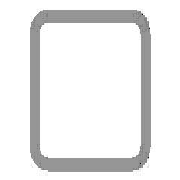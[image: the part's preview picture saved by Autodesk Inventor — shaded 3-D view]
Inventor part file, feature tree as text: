
AUTODESK INVENTOR PART (.ipt)
format: ipt  version: 2024 (Build 280153000, 153)  size: 128,512 bytes
history: native  units: mm (DEFAULTED — no unit token found)
features: other x4, extrude x1, sketch x1, plane x1
ambient origin geometry x8: Origin, YZ Plane, XZ Plane, XY Plane, X Axis, Y Axis, Z Axis, Center Point
bodies: Solid1 (feature_tree)
feature tree (7):
  parser-record x1  (decoder bookkeeping rows leaked as tree rows — omitted from the tree; the rows remain in map.json)
  other  "Driven Length"
  other  "Plano inicial"
  other  "Plano final"
  extrude  "Cuerpo"  TaperAngle=0.0deg  [1 undecoded]
  sketch  "Sketch3"  dims[d3=2890.0mm d4=0.0mm d10=50.8mm d11=50.8mm d12=3.175mm d13=-0.0mm d14=2890.0mm d15=25.4mm d16=25.4mm d17=6.35mm d18=90.0deg d19=2890.0mm]
  plane  "Work Plane3"
note: 1 required parameter value undecoded (feature->parameter linkage not recoverable at this tier; creation-order binding heuristic only, values carry confidence <= 0.55)
